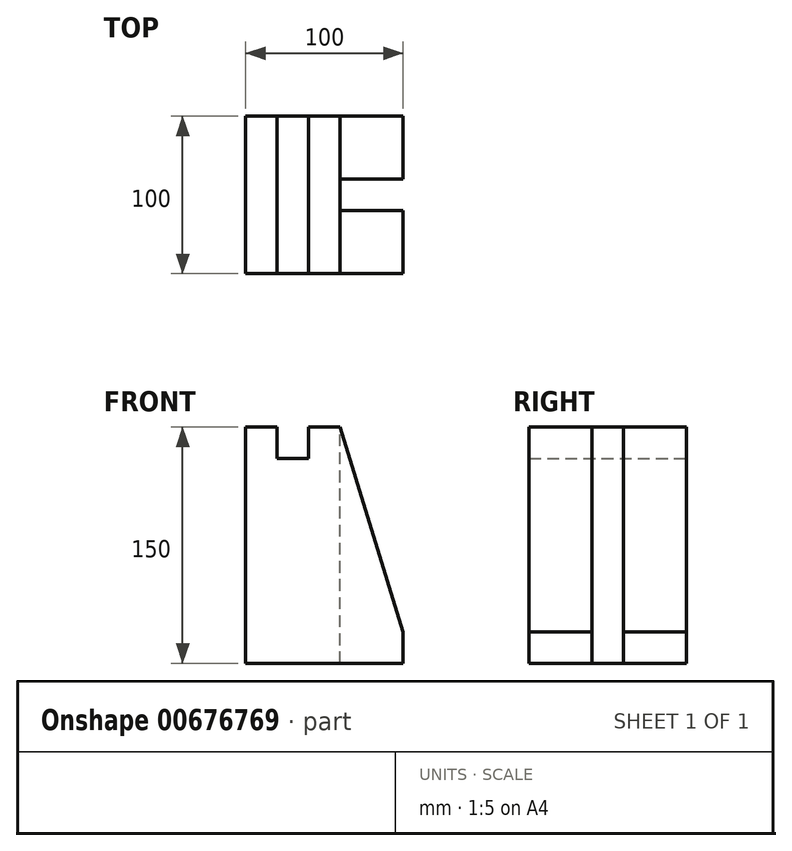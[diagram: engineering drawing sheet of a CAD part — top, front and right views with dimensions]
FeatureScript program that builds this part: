
annotation { "Feature Type Name" : "Feature", "Feature Type Description" : "" }
export const myFeature = defineFeature(function(context is Context, id is Id, definition is map)
    precondition{}
    {
        {
            var Q0;
            Q0=qCreatedBy(makeId("Front.planeOp"),FACE);
            var sketch = newSketch(context, id + "F0", { "sketchPlane" : qUnion([Q0])});
            skLineSegment(sketch, "E0", {"start": v(0, 0) * mm, "end": v(100, 0) * mm});
            skLineSegment(sketch, "E1", {"start": v(0, 0) * mm, "end": v(0, 150) * mm});
            skLineSegment(sketch, "E2", {"start": v(0, 150) * mm, "end": v(20, 150) * mm});
            skLineSegment(sketch, "E3", {"start": v(20, 150) * mm, "end": v(20, 130) * mm});
            skLineSegment(sketch, "E4", {"start": v(20, 130) * mm, "end": v(40, 130) * mm});
            skLineSegment(sketch, "E5", {"start": v(40, 130) * mm, "end": v(40, 150) * mm});
            skLineSegment(sketch, "E6", {"start": v(40, 150) * mm, "end": v(60, 150) * mm});
            skLineSegment(sketch, "E7", {"start": v(100, 0) * mm, "end": v(100, 20) * mm});
            skLineSegment(sketch, "E8", {"start": v(100, 20) * mm, "end": v(60, 150) * mm});
            skSolve(sketch);
        }
        {
            var Q0;
            Q0=makeQuery(id+"F0.imprint","IMPRINT",FACE,{"disambiguationData":[TD([[makeQuery(id+"F0.imprint","IMPRINT",EDGE,{"derivedFrom":sQuery(id+"F0.wireOp",EDGE,"E0")}),1.0]])]});
            extrude(context, id + "F1", {"entities" : qUnion([Q0]), "depth" : 100 * mm, "offsetDistance" : 25 * mm});
        }
        {
            var Q0;
            Q0=makeQuery(id+"F1.opExtrude","SWEPT_FACE",FACE,{"disambiguationData":[OSD([sQuery(id+"F0.wireOp",EDGE,"E6")])]});
            var sketch = newSketch(context, id + "F2", { "sketchPlane" : qUnion([Q0])});
            skLineSegment(sketch, "E9", {"start": v(60, -60) * mm, "end": v(50, -60) * mm});
            skLineSegment(sketch, "E10", {"start": v(50, -60) * mm, "end": v(50, -40) * mm});
            skLineSegment(sketch, "E11", {"start": v(50, -40) * mm, "end": v(60, -40) * mm});
            skLineSegment(sketch, "E12.bottom", {"start": v(50, -40) * mm, "end": v(167.06, -40) * mm});
            skLineSegment(sketch, "E12.top", {"start": v(50, -60) * mm, "end": v(167.06, -60) * mm});
            skLineSegment(sketch, "E12.left", {"start": v(50, -40) * mm, "end": v(50, -60) * mm});
            skLineSegment(sketch, "E12.right", {"start": v(167.06, -40) * mm, "end": v(167.06, -60) * mm});
            skSolve(sketch);
        }
        {
            var Q0;
            {var subQ0=sQuery(id+"F2.wireOp",EDGE,"E12.right");Q0=makeQuery(id+"F2.imprint","IMPRINT",FACE,{"disambiguationData":[TD([[makeQuery(id+"F2.imprint","IMPRINT",EDGE,{"derivedFrom":subQ0}),-1.0]])]});}
            var Q1;
            {var subQ0=sQuery(id+"F2.wireOp",EDGE,"E12.left");Q1=makeQuery(id+"F2.imprint","IMPRINT",FACE,{"disambiguationData":[TD([[makeQuery(id+"F2.imprint","IMPRINT",EDGE,{"derivedFrom":subQ0}),1.0]])]});}
            extrude(context, id + "F3", {"entities" : qUnion([Q0, Q1]), "operationType" : NewBodyOperationType.REMOVE, "oppositeDirection" : true, "depth" : 150 * mm, "offsetDistance" : 25 * mm});
        }
    });
